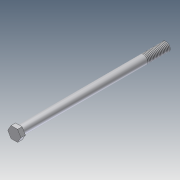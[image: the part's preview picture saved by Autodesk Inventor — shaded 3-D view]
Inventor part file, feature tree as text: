
AUTODESK INVENTOR PART (.ipt)
format: ipt  version: 2012 (Build 160160000, 160)  size: 81,408 bytes
history: native  units: in
note: dims shown in document units (in); Inventor stores cm internally (conversion verified against a paired STEP export)
features: extrude x2, sketch x1, thread x1
ambient origin geometry x8: Origin, YZ Plane, XZ Plane, XY Plane, X Axis, Y Axis, Z Axis, Center Point
bodies: Solid1 (feature_tree)
feature tree (4):
  sketch  "Sketch1"  dims[d10=0.5in d11=6.5in d12=0.0in d13=0.2in d14=0.0in d20=0.375in d21=1.0in d22=0.0in]
  extrude  "Extrusion1"  Depth=6.5in TaperAngle=0.0deg
  extrude  "Extrusion2"  Depth=0.2in TaperAngle=0.0deg
  thread  "Thread2"  [1 undecoded]
note: 1 required parameter value undecoded (feature->parameter linkage not recoverable at this tier; creation-order binding heuristic only, values carry confidence <= 0.55)
